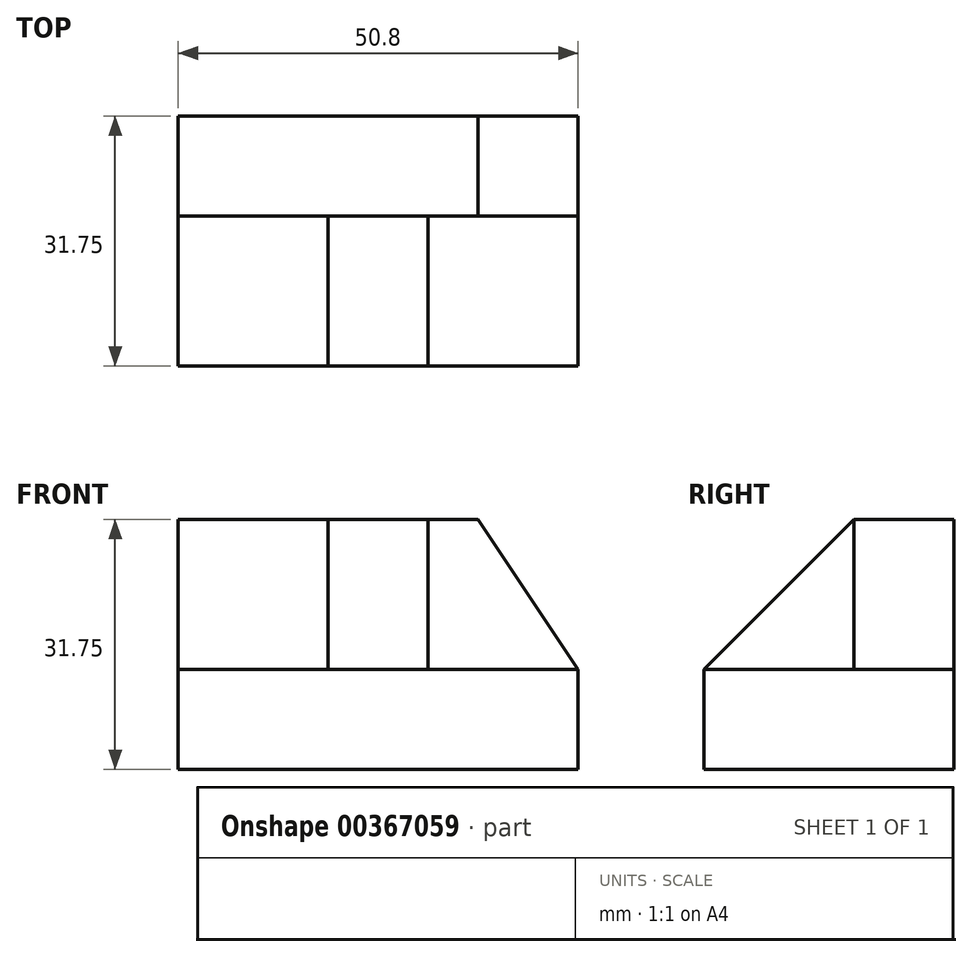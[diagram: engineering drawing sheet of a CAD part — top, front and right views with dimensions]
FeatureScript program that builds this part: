
annotation { "Feature Type Name" : "Feature", "Feature Type Description" : "" }
export const myFeature = defineFeature(function(context is Context, id is Id, definition is map)
    precondition{}
    {
        {
            var Q0;
            Q0=qCreatedBy(makeId("Front.planeOp"),FACE);
            var sketch = newSketch(context, id + "F0", { "sketchPlane" : qUnion([Q0])});
            skLineSegment(sketch, "E0", {"start": v(-50.8, 0) * mm, "end": v(0, 0) * mm});
            skLineSegment(sketch, "E1", {"start": v(0, 0) * mm, "end": v(0, 31.75) * mm});
            skLineSegment(sketch, "E2", {"start": v(0, 31.75) * mm, "end": v(-50.8, 31.75) * mm});
            skLineSegment(sketch, "E3", {"start": v(-50.8, 31.75) * mm, "end": v(-50.8, 0) * mm});
            skSolve(sketch);
        }
        {
            var Q0;
            Q0=makeQuery(id+"F0.imprint","IMPRINT",FACE,{"disambiguationData":[TD([[makeQuery(id+"F0.imprint","IMPRINT",EDGE,{"derivedFrom":sQuery(id+"F0.wireOp",EDGE,"E0")}),1.0]])]});
            extrude(context, id + "F1", {"entities" : qUnion([Q0]), "depth" : 31.75 * mm});
        }
        {
            var Q0;
            Q0=makeQuery(id+"F1.opExtrude","CAP_FACE",FACE,{"disambiguationData":[OSD([sQuery(id+"F0.wireOp",EDGE,"E0"),sQuery(id+"F0.wireOp",EDGE,"E1"),sQuery(id+"F0.wireOp",EDGE,"E2"),sQuery(id+"F0.wireOp",EDGE,"E3")])],"isStart":true});
            var sketch = newSketch(context, id + "F2", { "sketchPlane" : qUnion([Q0])});
            skLineSegment(sketch, "E4", {"start": v(0, 12.7) * mm, "end": v(12.7, 31.75) * mm});
            skLineSegment(sketch, "E5", {"start": v(0, 12.7) * mm, "end": v(0, 31.75) * mm});
            skLineSegment(sketch, "E6", {"start": v(0, 31.75) * mm, "end": v(12.7, 31.75) * mm});
            skSolve(sketch);
        }
        {
            var Q0;
            Q0=makeQuery(id+"F2.imprint","IMPRINT",FACE,{"disambiguationData":[TD([[makeQuery(id+"F2.imprint","IMPRINT",EDGE,{"derivedFrom":sQuery(id+"F2.wireOp",EDGE,"E4")}),1.0]])]});
            extrude(context, id + "F3", {"entities" : qUnion([Q0]), "operationType" : NewBodyOperationType.REMOVE, "oppositeDirection" : true, "depth" : 12.7 * mm});
        }
        {
            var Q0;
            Q0=makeQuery(id+"F1.opExtrude","CAP_FACE",FACE,{"disambiguationData":[OSD([sQuery(id+"F0.wireOp",EDGE,"E0"),sQuery(id+"F0.wireOp",EDGE,"E1"),sQuery(id+"F0.wireOp",EDGE,"E2"),sQuery(id+"F0.wireOp",EDGE,"E3")])],"isStart":false});
            var sketch = newSketch(context, id + "F4", { "sketchPlane" : qUnion([Q0])});
            skLineSegment(sketch, "E7", {"start": v(-19.05, 12.7) * mm, "end": v(0, 12.7) * mm});
            skLineSegment(sketch, "E8", {"start": v(0, 12.7) * mm, "end": v(0, 31.75) * mm});
            skLineSegment(sketch, "E9", {"start": v(-19.05, 12.7) * mm, "end": v(-19.05, 31.75) * mm});
            skLineSegment(sketch, "E10", {"start": v(-19.05, 31.75) * mm, "end": v(0, 31.75) * mm});
            skSolve(sketch);
        }
        {
            var Q0;
            Q0=makeQuery(id+"F4.imprint","IMPRINT",FACE,{"disambiguationData":[TD([[makeQuery(id+"F4.imprint","IMPRINT",EDGE,{"derivedFrom":sQuery(id+"F4.wireOp",EDGE,"E7")}),1.0]])]});
            extrude(context, id + "F5", {"entities" : qUnion([Q0]), "operationType" : NewBodyOperationType.REMOVE, "oppositeDirection" : true, "depth" : 19.05 * mm});
        }
        {
            var Q0;
            Q0=makeQuery(id+"F5.boolean.opBoolean","COPY",FACE,{"derivedFrom":makeQuery(id+"F5.opExtrude","SWEPT_FACE",FACE,{"disambiguationData":[OSD([sQuery(id+"F4.wireOp",EDGE,"E9")])]})});
            var sketch = newSketch(context, id + "F6", { "sketchPlane" : qUnion([Q0])});
            skLineSegment(sketch, "E11", {"start": v(-31.75, 12.7) * mm, "end": v(-12.7, 31.75) * mm});
            skLineSegment(sketch, "E12", {"start": v(-31.75, 12.7) * mm, "end": v(-31.75, 31.75) * mm});
            skLineSegment(sketch, "E13", {"start": v(-31.75, 31.75) * mm, "end": v(-12.7, 31.75) * mm});
            skSolve(sketch);
        }
        {
            var Q0;
            Q0=makeQuery(id+"F6.imprint","IMPRINT",FACE,{"disambiguationData":[TD([[makeQuery(id+"F6.imprint","IMPRINT",EDGE,{"derivedFrom":sQuery(id+"F6.wireOp",EDGE,"E11")}),1.0]])]});
            extrude(context, id + "F7", {"entities" : qUnion([Q0]), "operationType" : NewBodyOperationType.REMOVE, "oppositeDirection" : true, "depth" : 12.7 * mm});
        }
        {
            var Q0;
            Q0=makeQuery(id+"F1.opExtrude","CAP_FACE",FACE,{"disambiguationData":[OSD([sQuery(id+"F0.wireOp",EDGE,"E0"),sQuery(id+"F0.wireOp",EDGE,"E1"),sQuery(id+"F0.wireOp",EDGE,"E2"),sQuery(id+"F0.wireOp",EDGE,"E3")])],"isStart":false});
            var sketch = newSketch(context, id + "F8", { "sketchPlane" : qUnion([Q0])});
            skLineSegment(sketch, "E14", {"start": v(-50.8, 12.7) * mm, "end": v(-31.75, 12.7) * mm});
            skLineSegment(sketch, "E15", {"start": v(-31.75, 12.7) * mm, "end": v(-31.75, 31.75) * mm});
            skLineSegment(sketch, "E16", {"start": v(-31.75, 31.75) * mm, "end": v(-50.8, 31.75) * mm});
            skLineSegment(sketch, "E17", {"start": v(-50.8, 31.75) * mm, "end": v(-50.8, 12.7) * mm});
            skSolve(sketch);
        }
        {
            var Q0;
            Q0=makeQuery(id+"F8.imprint","IMPRINT",FACE,{"disambiguationData":[TD([[makeQuery(id+"F8.imprint","IMPRINT",EDGE,{"derivedFrom":sQuery(id+"F8.wireOp",EDGE,"E14")}),1.0]])]});
            extrude(context, id + "F9", {"entities" : qUnion([Q0]), "operationType" : NewBodyOperationType.REMOVE, "oppositeDirection" : true, "depth" : 19.05 * mm});
        }
    });
